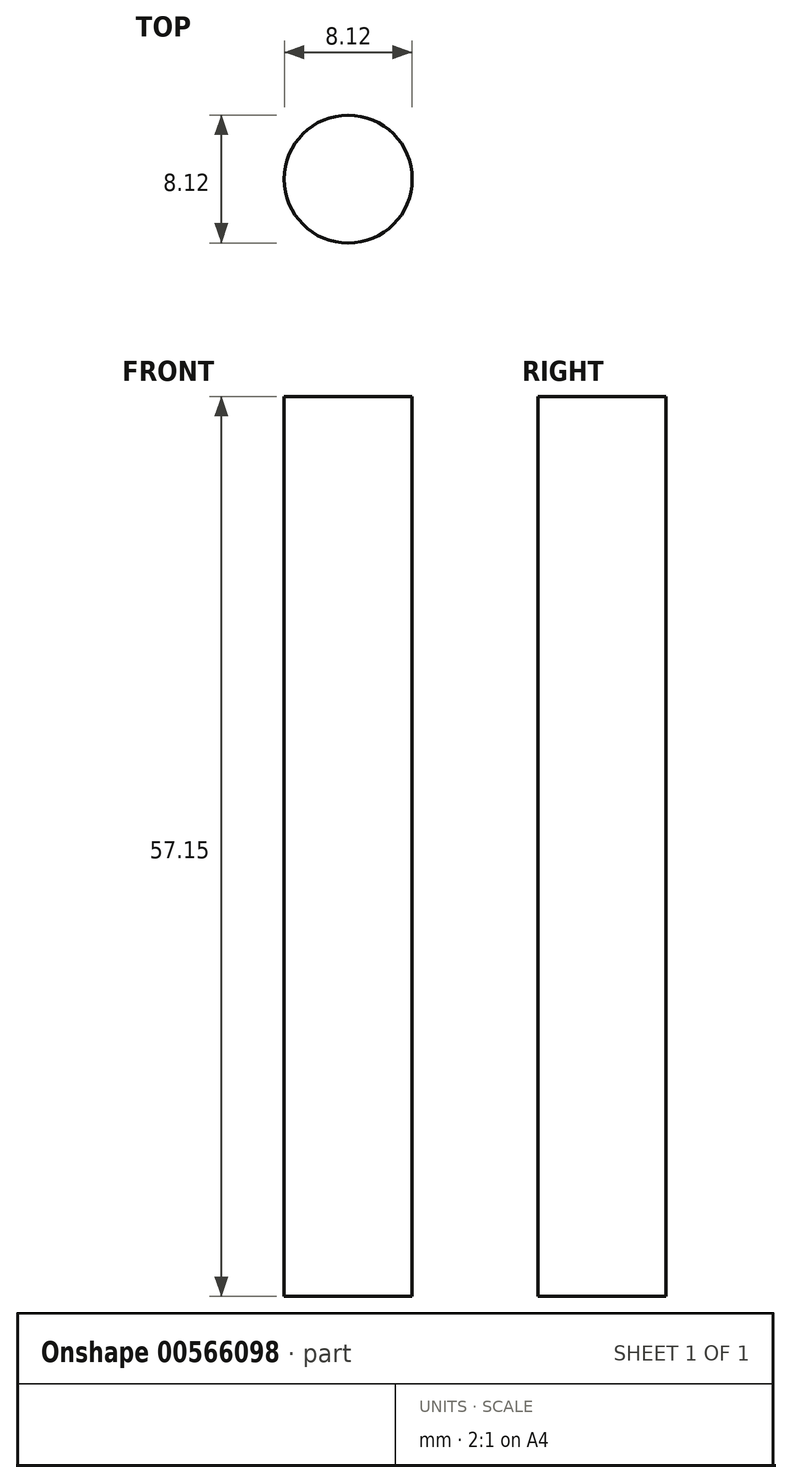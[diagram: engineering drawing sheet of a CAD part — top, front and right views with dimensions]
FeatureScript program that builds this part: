
annotation { "Feature Type Name" : "Feature", "Feature Type Description" : "" }
export const myFeature = defineFeature(function(context is Context, id is Id, definition is map)
    precondition{}
    {
        {
            var Q0;
            Q0=qCreatedBy(makeId("Top.planeOp"),FACE);
            var sketch = newSketch(context, id + "F0", { "sketchPlane" : qUnion([Q0])});
            skCircle(sketch, "E0", {"center": v(0, 0) * mm, "radius": 4.06 * mm});
            skSolve(sketch);
        }
        {
            var Q0;
            Q0 = qSketchRegion(id + "F0", true);
            extrude(context, id + "F1", {"entities" : qUnion([Q0]), "depth" : 57.15 * mm, "offsetDistance" : 25.4 * mm});
        }
    });
